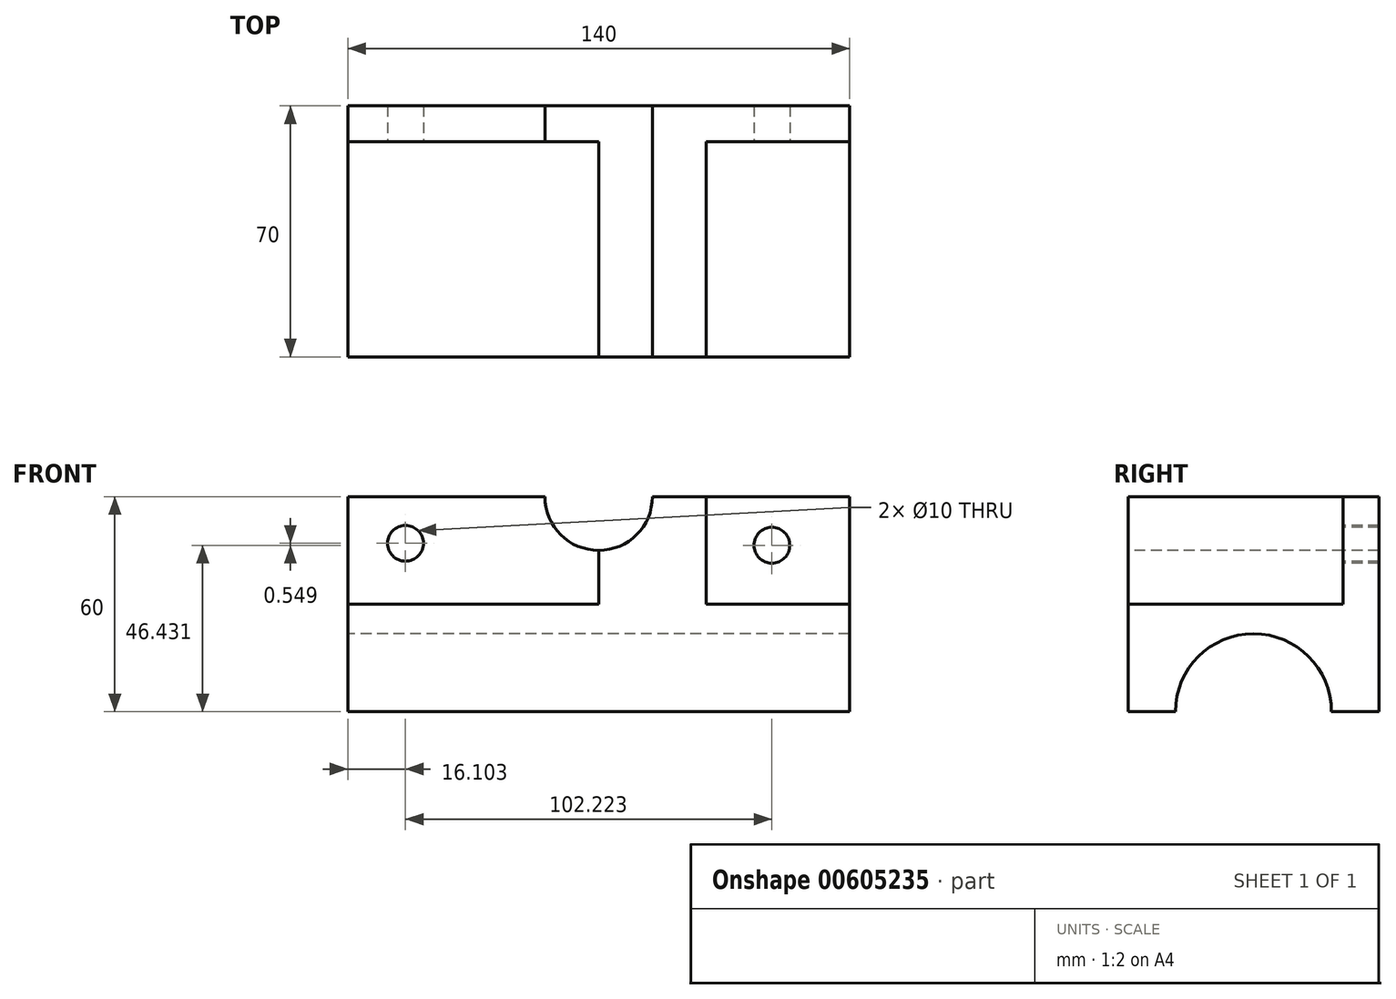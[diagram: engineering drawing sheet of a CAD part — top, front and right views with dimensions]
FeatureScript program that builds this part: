
annotation { "Feature Type Name" : "Feature", "Feature Type Description" : "" }
export const myFeature = defineFeature(function(context is Context, id is Id, definition is map)
    precondition{}
    {
        {
            var Q0;
            Q0=qCreatedBy(makeId("Right.planeOp"),FACE);
            var sketch = newSketch(context, id + "F0", { "sketchPlane" : qUnion([Q0])});
            skLineSegment(sketch, "E0", {"start": v(0, 30) * mm, "end": v(0, 0) * mm});
            skLineSegment(sketch, "E1", {"start": v(0, 0) * mm, "end": v(-60, 0) * mm});
            skLineSegment(sketch, "E2", {"start": v(-60, 0) * mm, "end": v(-60, -30) * mm});
            skLineSegment(sketch, "E3", {"start": v(-60, -30) * mm, "end": v(10, -30) * mm, "construction": true});
            skLineSegment(sketch, "E4", {"start": v(10, -30) * mm, "end": v(10, 30) * mm});
            skLineSegment(sketch, "E5", {"start": v(10, 30) * mm, "end": v(0, 30) * mm});
            skPoint(sketch, "E6", {"position": v(-25, -30) * mm});
            skArc(sketch, "E7", {"start": v(-3.25, -30) * mm, "mid": v(-25, -8.25) * mm, "end": v(-46.75, -30) * mm});
            skPoint(sketch, "E8", {"position": v(-46.75, -30) * mm});
            skPoint(sketch, "E9", {"position": v(-3.25, -30) * mm});
            skLineSegment(sketch, "E10", {"start": v(-60, -30) * mm, "end": v(-46.75, -30) * mm});
            skLineSegment(sketch, "E11", {"start": v(-3.25, -30) * mm, "end": v(10, -30) * mm});
            skSolve(sketch);
        }
        {
            var Q0;
            Q0 = qSketchRegion(id + "F0", true);
            extrude(context, id + "F1", {"entities" : qUnion([Q0]), "depth" : 140 * mm, "offsetDistance" : 25 * mm, "symmetric" : true});
        }
        {
            var Q0;
            Q0=makeQuery(id+"F1.opExtrude","SWEPT_FACE",FACE,{"disambiguationData":[OSD([sQuery(id+"F0.wireOp",EDGE,"E0")])]});
            var sketch = newSketch(context, id + "F2", { "sketchPlane" : qUnion([Q0])});
            skLineSegment(sketch, "E12", {"start": v(0, 30) * mm, "end": v(0, 0) * mm});
            skLineSegment(sketch, "E13", {"start": v(0, 0) * mm, "end": v(30, 0) * mm});
            skLineSegment(sketch, "E14", {"start": v(30, 0) * mm, "end": v(30, 30) * mm});
            skLineSegment(sketch, "E15", {"start": v(30, 30) * mm, "end": v(0, 30) * mm});
            skSolve(sketch);
        }
        {
            var Q0;
            Q0 = qSketchRegion(id + "F2", true);
            var Q1;
            Q1=makeQuery(id+"F1.opExtrude","SWEPT_FACE",FACE,{"disambiguationData":[OSD([sQuery(id+"F0.wireOp",EDGE,"E2")])]});
            extrude(context, id + "F3", {"entities" : qUnion([Q0]), "operationType" : NewBodyOperationType.ADD, "endBound" : BoundingType.UP_TO_SURFACE, "depth" : 60 * mm, "endBoundEntityFace" : qUnion([Q1]), "offsetDistance" : 25 * mm});
        }
        {
            var Q0;
            {var subQ0=sQuery(id+"F0.wireOp",EDGE,"E2");Q0=makeQuery(id+"FSl07YMLAUUbcol_1.1.F3.boolean.opBoolean","MERGE",FACE,{"derivedFrom":[makeQuery(id+"F3.boolean.opBoolean","MERGE",FACE,{"derivedFrom":[makeQuery(id+"F1.opExtrude","SWEPT_FACE",FACE,{"disambiguationData":[OSD([subQ0])]}),makeQuery(id+"F3.opExtrude","CAP_FACE",FACE,{"disambiguationData":[OSD([subQ0])],"isStart":false})]}),makeQuery(id+"FSl07YMLAUUbcol_1.1.F3.opExtrude","CAP_FACE",FACE,{"disambiguationData":[OSD([subQ0])],"isStart":false})]});}
            var sketch = newSketch(context, id + "F4", { "sketchPlane" : qUnion([Q0])});
            skCircle(sketch, "E16", {"center": v(0, 30) * mm, "radius": 15 * mm});
            skPoint(sketch, "E16.centerSnap0", {"position": v(0, 30) * mm});
            skSolve(sketch);
        }
        {
            var Q0;
            Q0 = qSketchRegion(id + "F4", true);
            extrude(context, id + "F5", {"entities" : qUnion([Q0]), "operationType" : NewBodyOperationType.REMOVE, "oppositeDirection" : true, "depth" : 72.5 * mm, "offsetDistance" : 25 * mm});
        }
        {
            var Q0;
            {var subQ2=sQuery(id+"F0.wireOp",EDGE,"E0");Q0=makeQuery(id+"F3.boolean.opBoolean","SPLIT",FACE,{"disambiguationData":[TD([makeQuery(id+"F3.opExtrude","SWEPT_FACE",FACE,{"disambiguationData":[OSD([sQuery(id+"F2.wireOp",EDGE,"E14")])]})])],"derivedFrom":makeQuery(id+"F1.opExtrude","SWEPT_FACE",FACE,{"disambiguationData":[OSD([subQ2])]})});}
            var sketch = newSketch(context, id + "F6", { "sketchPlane" : qUnion([Q0])});
            skCircle(sketch, "E17", {"center": v(48.33, 16.43) * mm, "radius": 5 * mm});
            skSolve(sketch);
        }
        {
            var Q0;
            Q0 = qSketchRegion(id + "F6", true);
            extrude(context, id + "F7", {"entities" : qUnion([Q0]), "operationType" : NewBodyOperationType.REMOVE, "oppositeDirection" : true, "depth" : 37.8 * mm, "offsetDistance" : 25 * mm});
        }
        {
            var Q0;
            {var subQ2=sQuery(id+"F0.wireOp",EDGE,"E0");Q0=makeQuery(id+"F3.boolean.opBoolean","SPLIT",FACE,{"disambiguationData":[TD([makeQuery(id+"F3.opExtrude","SWEPT_FACE",FACE,{"disambiguationData":[OSD([sQuery(id+"F2.wireOp",EDGE,"E12")])]})])],"derivedFrom":makeQuery(id+"F1.opExtrude","SWEPT_FACE",FACE,{"disambiguationData":[OSD([subQ2])]})});}
            var sketch = newSketch(context, id + "F8", { "sketchPlane" : qUnion([Q0])});
            skCircle(sketch, "E18", {"center": v(-53.9, 16.98) * mm, "radius": 5 * mm});
            skSolve(sketch);
        }
        {
            var Q0;
            Q0 = qSketchRegion(id + "F8", true);
            extrude(context, id + "F9", {"entities" : qUnion([Q0]), "operationType" : NewBodyOperationType.REMOVE, "oppositeDirection" : true, "depth" : 25 * mm, "offsetDistance" : 25 * mm});
        }
    });
